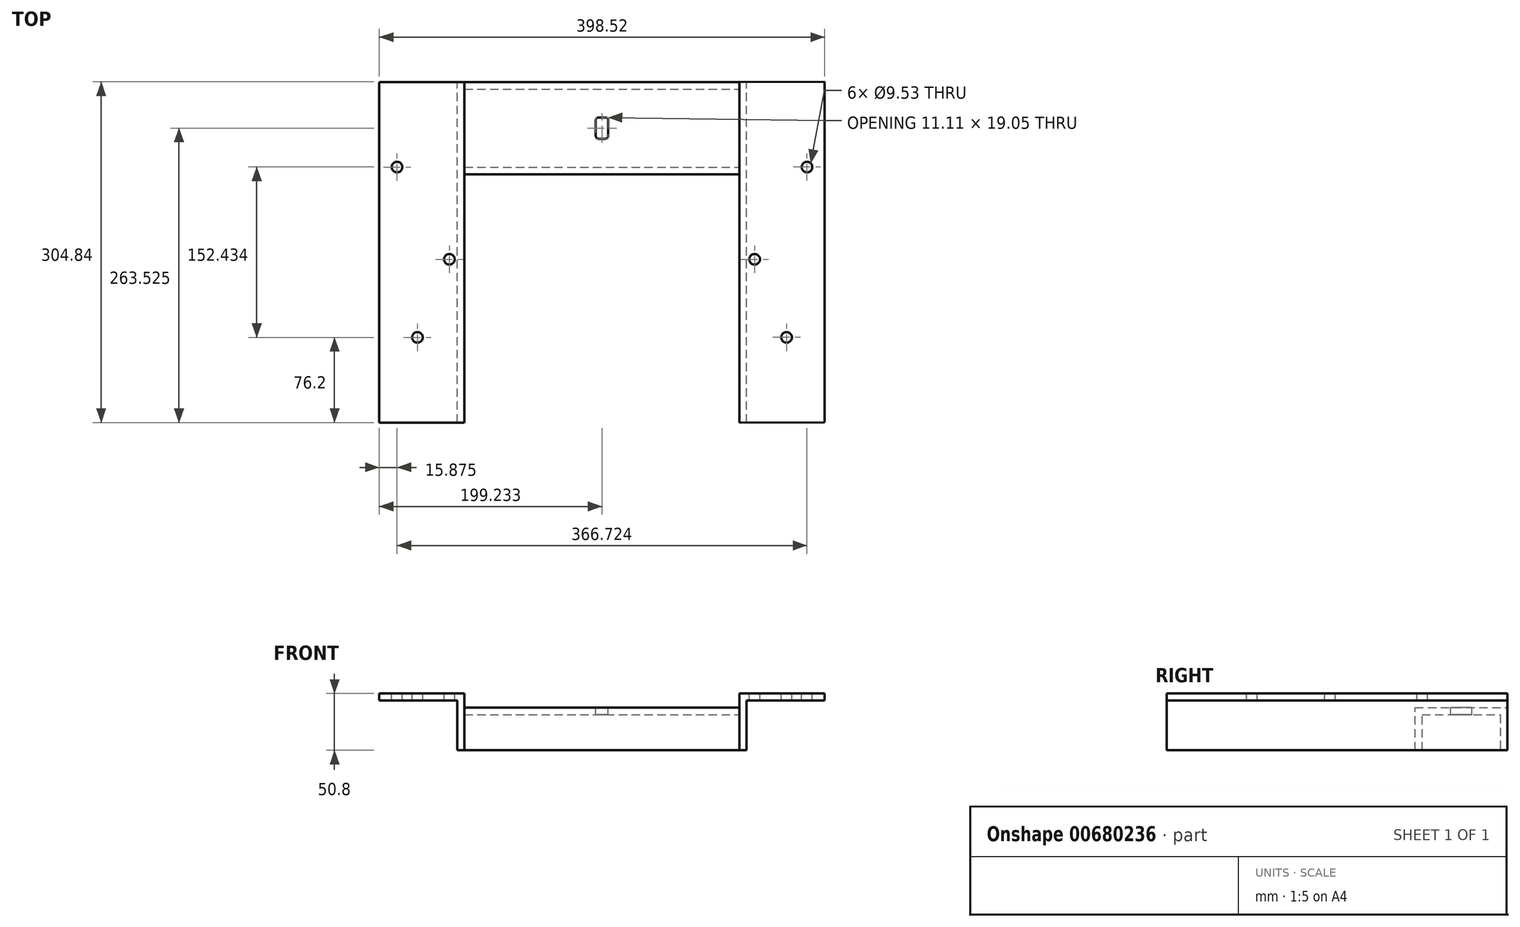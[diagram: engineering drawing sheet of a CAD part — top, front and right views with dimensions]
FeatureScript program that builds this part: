
annotation { "Feature Type Name" : "Feature", "Feature Type Description" : "" }
export const myFeature = defineFeature(function(context is Context, id is Id, definition is map)
    precondition{}
    {
        {
            var Q0;
            Q0=qCreatedBy(makeId("Front.planeOp"),FACE);
            var sketch = newSketch(context, id + "F0", { "sketchPlane" : qUnion([Q0])});
            skLineSegment(sketch, "E0", {"start": v(0, 0) * mm, "end": v(0, -50.8) * mm});
            skLineSegment(sketch, "E1", {"start": v(0, 0) * mm, "end": v(-76.2, 0) * mm});
            skLineSegment(sketch, "E2", {"start": v(-76.2, 0) * mm, "end": v(-76.2, -6.35) * mm});
            skLineSegment(sketch, "E3", {"start": v(-76.2, -6.35) * mm, "end": v(-6.35, -6.35) * mm});
            skLineSegment(sketch, "E4", {"start": v(-6.35, -6.35) * mm, "end": v(-6.35, -50.8) * mm});
            skLineSegment(sketch, "E5", {"start": v(-6.35, -50.8) * mm, "end": v(0, -50.8) * mm});
            skSolve(sketch);
        }
        {
            var Q0;
            Q0 = qSketchRegion(id + "F0", true);
            extrude(context, id + "F1", {"entities" : qUnion([Q0]), "depth" : 304.8 * mm, "offsetDistance" : 25.4 * mm});
        }
        {
            var Q0;
            Q0=makeQuery(id+"F1.opExtrude","SWEPT_FACE",FACE,{"disambiguationData":[OSD([sQuery(id+"F0.wireOp",EDGE,"E1")])]});
            var sketch = newSketch(context, id + "F2", { "sketchPlane" : qUnion([Q0])});
            skLineSegment(sketch, "E6", {"start": v(-76.2, 0) * mm, "end": v(-76.2, -76.2) * mm});
            skLineSegment(sketch, "E7", {"start": v(-76.2, -76.2) * mm, "end": v(-76.2, -158.75) * mm});
            skLineSegment(sketch, "E8", {"start": v(-76.2, -158.75) * mm, "end": v(-76.2, -228.6) * mm});
            skLineSegment(sketch, "E9", {"start": v(-76.2, -76.2) * mm, "end": v(-60.33, -76.2) * mm});
            skCircle(sketch, "E10", {"center": v(-60.33, -76.2) * mm, "radius": 4.76 * mm});
            skLineSegment(sketch, "E11", {"start": v(-76.2, -158.75) * mm, "end": v(-13.5, -158.75) * mm});
            skCircle(sketch, "E12", {"center": v(-13.5, -158.75) * mm, "radius": 4.76 * mm});
            skLineSegment(sketch, "E13", {"start": v(-76.2, -228.6) * mm, "end": v(-42.07, -228.6) * mm});
            skCircle(sketch, "E14", {"center": v(-42.07, -228.6) * mm, "radius": 4.76 * mm});
            skSolve(sketch);
        }
        {
            var Q0;
            Q0 = qSketchRegion(id + "F2", true);
            extrude(context, id + "F3", {"entities" : qUnion([Q0]), "operationType" : NewBodyOperationType.REMOVE, "oppositeDirection" : true, "depth" : 6.35 * mm, "offsetDistance" : 25.4 * mm});
        }
        {
            var Q0;
            Q0=makeQuery(id+"F1.opExtrude","SWEPT_FACE",FACE,{"disambiguationData":[OSD([sQuery(id+"F0.wireOp",EDGE,"E1")])]});
            var sketch = newSketch(context, id + "F4", { "sketchPlane" : qUnion([Q0])});
            skLineSegment(sketch, "E15", {"start": v(0, 0) * mm, "end": v(123.03, 0) * mm});
            skLineSegment(sketch, "E16", {"start": v(0, 0) * mm, "end": v(0, -6.35) * mm});
            skLineSegment(sketch, "E17", {"start": v(0, -6.35) * mm, "end": v(0, -82.55) * mm});
            skLineSegment(sketch, "E18", {"start": v(0, -82.55) * mm, "end": v(123.04, -82.55) * mm});
            skLineSegment(sketch, "E19", {"start": v(123.04, -82.55) * mm, "end": v(123.03, 0) * mm});
            skSolve(sketch);
        }
        {
            var Q0;
            Q0 = qSketchRegion(id + "F4", true);
            extrude(context, id + "F5", {"entities" : qUnion([Q0]), "oppositeDirection" : true, "depth" : 50.8 * mm, "offsetDistance" : 25.4 * mm});
        }
        {
            var Q0;
            Q0=makeQuery(id+"F5.opExtrude","CAP_FACE",FACE,{"disambiguationData":[OSD([sQuery(id+"F4.wireOp",EDGE,"E15"),sQuery(id+"F4.wireOp",EDGE,"E16"),sQuery(id+"F4.wireOp",EDGE,"E17"),sQuery(id+"F4.wireOp",EDGE,"E18"),sQuery(id+"F4.wireOp",EDGE,"E19")])],"isStart":true});
            extrude(context, id + "F6", {"entities" : qUnion([Q0]), "operationType" : NewBodyOperationType.REMOVE, "oppositeDirection" : true, "depth" : 12.7 * mm, "offsetDistance" : 25.4 * mm});
        }
        {
            var Q0;
            Q0=makeQuery(id+"F5.opExtrude","SWEPT_FACE",FACE,{"disambiguationData":[OSD([sQuery(id+"F4.wireOp",EDGE,"E19")])]});
            var sketch = newSketch(context, id + "F7", { "sketchPlane" : qUnion([Q0])});
            skLineSegment(sketch, "E20", {"start": v(-76.21, -50.8) * mm, "end": v(-76.21, -19.05) * mm});
            skLineSegment(sketch, "E21", {"start": v(-76.21, -19.05) * mm, "end": v(-6.36, -19.05) * mm});
            skLineSegment(sketch, "E22", {"start": v(-6.36, -19.05) * mm, "end": v(-6.36, -50.8) * mm});
            skLineSegment(sketch, "E23", {"start": v(-6.36, -50.8) * mm, "end": v(-76.21, -50.8) * mm});
            skSolve(sketch);
        }
        {
            var Q0;
            Q0=makeQuery(id+"F7.imprint","IMPRINT",FACE,{"disambiguationData":[TD([[makeQuery(id+"F7.imprint","IMPRINT",EDGE,{"derivedFrom":sQuery(id+"F7.wireOp",EDGE,"E20")}),-1.0]])]});
            extrude(context, id + "F8", {"entities" : qUnion([Q0]), "operationType" : NewBodyOperationType.REMOVE, "oppositeDirection" : true, "depth" : 123.04 * mm, "offsetDistance" : 25.4 * mm});
        }
        {
            var Q0;
            Q0=makeQuery(id+"F1.opExtrude","SWEPT_BODY",BODY,{"disambiguationData":[OSD([sQuery(id+"F0.wireOp",EDGE,"E0"),sQuery(id+"F0.wireOp",EDGE,"E1"),sQuery(id+"F0.wireOp",EDGE,"E2"),sQuery(id+"F0.wireOp",EDGE,"E3"),sQuery(id+"F0.wireOp",EDGE,"E4"),sQuery(id+"F0.wireOp",EDGE,"E5")])]});
            var Q1;
            Q1=makeQuery(id+"F5.opExtrude","SWEPT_BODY",BODY,{"disambiguationData":[OSD([sQuery(id+"F4.wireOp",EDGE,"E15"),sQuery(id+"F4.wireOp",EDGE,"E16"),sQuery(id+"F4.wireOp",EDGE,"E17"),sQuery(id+"F4.wireOp",EDGE,"E18"),sQuery(id+"F4.wireOp",EDGE,"E19")])]});
            var Q2;
            Q2=makeQuery(id+"F5.opExtrude","SWEPT_FACE",FACE,{"disambiguationData":[OSD([sQuery(id+"F4.wireOp",EDGE,"E19")])]});
            mirror(context, id + "F9", {"operationType" : NewBodyOperationType.ADD, "entities" : qUnion([Q0, Q1]), "mirrorPlane" : qUnion([Q2])});
        }
        {
            var Q0;
            {var subQ0=makeQuery(id+"F6.boolean.opBoolean","COPY",FACE,{"derivedFrom":makeQuery(id+"F6.opExtrude","CAP_FACE",FACE,{"disambiguationData":[OSD([sQuery(id+"F4.wireOp",EDGE,"E15"),sQuery(id+"F4.wireOp",EDGE,"E16"),sQuery(id+"F4.wireOp",EDGE,"E17"),sQuery(id+"F4.wireOp",EDGE,"E18"),sQuery(id+"F4.wireOp",EDGE,"E19")])],"isStart":false})});Q0=makeQuery(id+"F9.boolean.opBoolean","MERGE",FACE,{"derivedFrom":[subQ0,makeQuery(id+"F9.opPattern","COPY",FACE,{"derivedFrom":subQ0,"instanceName":"1"})]});}
            var sketch = newSketch(context, id + "F10", { "sketchPlane" : qUnion([Q0])});
            skLineSegment(sketch, "E24", {"start": v(128.59, -41.27) * mm, "end": v(128.59, -48.26) * mm});
            skLineSegment(sketch, "E25", {"start": v(126.05, -50.8) * mm, "end": v(120.02, -50.8) * mm});
            skLineSegment(sketch, "E26", {"start": v(117.48, -48.26) * mm, "end": v(117.48, -34.3) * mm});
            skLineSegment(sketch, "E27", {"start": v(120.02, -31.75) * mm, "end": v(126.05, -31.75) * mm});
            skLineSegment(sketch, "E28", {"start": v(128.59, -34.29) * mm, "end": v(128.59, -41.27) * mm});
            skPoint(sketch, "E29.visualSharp", {"position": v(117.48, -31.75) * mm});
            skArc(sketch, "E29.filletArc", {"start": v(120.02, -31.75) * mm, "mid": v(118.22, -32.5) * mm, "end": v(117.48, -34.3) * mm});
            skPoint(sketch, "E30.visualSharp", {"position": v(128.59, -31.75) * mm});
            skArc(sketch, "E30.filletArc", {"start": v(128.59, -34.29) * mm, "mid": v(127.85, -32.5) * mm, "end": v(126.05, -31.75) * mm});
            skPoint(sketch, "E31.visualSharp", {"position": v(117.48, -50.8) * mm});
            skArc(sketch, "E31.filletArc", {"start": v(117.48, -48.26) * mm, "mid": v(118.22, -50.06) * mm, "end": v(120.02, -50.8) * mm});
            skPoint(sketch, "E32.visualSharp", {"position": v(128.59, -50.8) * mm});
            skArc(sketch, "E32.filletArc", {"start": v(126.05, -50.8) * mm, "mid": v(127.85, -50.06) * mm, "end": v(128.59, -48.26) * mm});
            skSolve(sketch);
        }
        {
            var Q0;
            Q0=makeQuery(id+"F10.imprint","IMPRINT",FACE,{"disambiguationData":[TD([[makeQuery(id+"F10.imprint","IMPRINT",EDGE,{"derivedFrom":sQuery(id+"F10.wireOp",EDGE,"E24")}),-1.0]])]});
            extrude(context, id + "F11", {"entities" : qUnion([Q0]), "operationType" : NewBodyOperationType.REMOVE, "oppositeDirection" : true, "depth" : 6.35 * mm, "offsetDistance" : 25.4 * mm});
        }
    });
